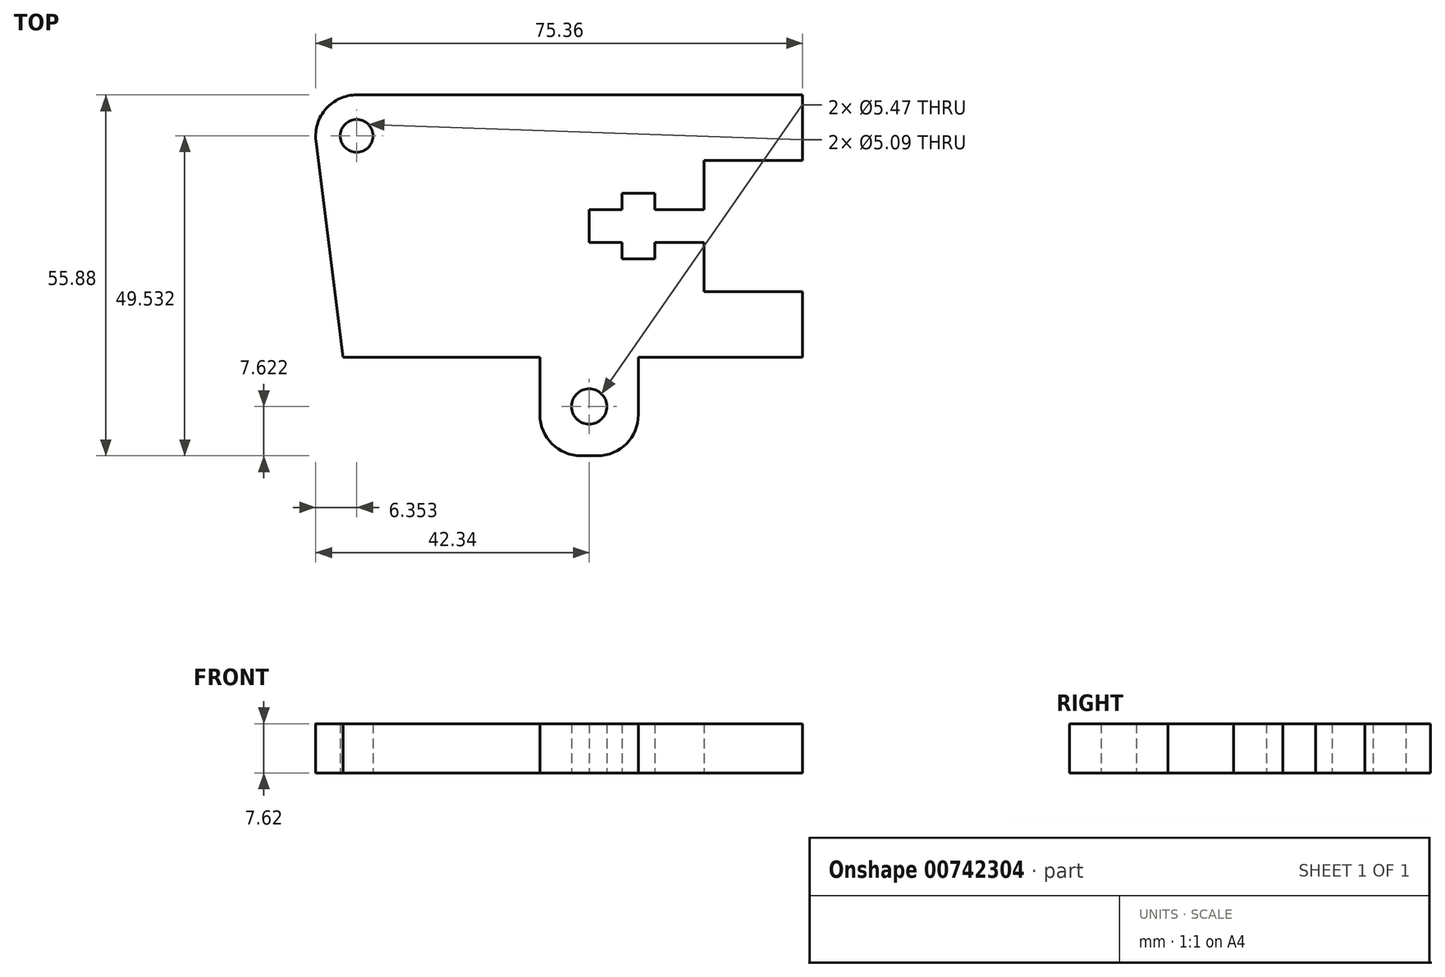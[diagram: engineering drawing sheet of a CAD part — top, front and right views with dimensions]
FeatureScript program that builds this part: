
annotation { "Feature Type Name" : "Feature", "Feature Type Description" : "" }
export const myFeature = defineFeature(function(context is Context, id is Id, definition is map)
    precondition{}
    {
        {
            var Q0;
            Q0=qCreatedBy(makeId("Top.planeOp"),FACE);
            var sketch = newSketch(context, id + "F0", { "sketchPlane" : qUnion([Q0])});
            skLineSegment(sketch, "E0", {"start": v(-53.77, 42.2) * mm, "end": v(15.24, 42.2) * mm});
            skLineSegment(sketch, "E1", {"start": v(15.24, 42.2) * mm, "end": v(15.24, 32.03) * mm});
            skLineSegment(sketch, "E2", {"start": v(15.24, 32.03) * mm, "end": v(0, 32.03) * mm});
            skLineSegment(sketch, "E3", {"start": v(0, 32.03) * mm, "end": v(0, 24.41) * mm});
            skLineSegment(sketch, "E4", {"start": v(0, 24.41) * mm, "end": v(-7.62, 24.41) * mm});
            skLineSegment(sketch, "E5", {"start": v(-12.7, 24.41) * mm, "end": v(-17.78, 24.41) * mm});
            skLineSegment(sketch, "E6", {"start": v(-17.78, 24.41) * mm, "end": v(-17.78, 19.33) * mm});
            skLineSegment(sketch, "E7", {"start": v(-17.78, 19.33) * mm, "end": v(-12.7, 19.33) * mm});
            skLineSegment(sketch, "E8", {"start": v(-12.7, 19.33) * mm, "end": v(-12.7, 16.8) * mm});
            skLineSegment(sketch, "E9", {"start": v(-12.7, 16.8) * mm, "end": v(-7.62, 16.8) * mm});
            skLineSegment(sketch, "E10", {"start": v(-7.62, 16.8) * mm, "end": v(-7.62, 19.33) * mm});
            skLineSegment(sketch, "E11", {"start": v(-7.62, 19.33) * mm, "end": v(0, 19.33) * mm});
            skLineSegment(sketch, "E12", {"start": v(0, 19.33) * mm, "end": v(0, 11.71) * mm});
            skLineSegment(sketch, "E13", {"start": v(0, 11.71) * mm, "end": v(15.24, 11.71) * mm});
            skLineSegment(sketch, "E14", {"start": v(15.24, 11.71) * mm, "end": v(15.24, 1.55) * mm});
            skLineSegment(sketch, "E15", {"start": v(15.24, 1.55) * mm, "end": v(-10.16, 1.55) * mm});
            skLineSegment(sketch, "E16", {"start": v(-10.16, 1.55) * mm, "end": v(-10.16, -7.34) * mm});
            skLineSegment(sketch, "E17", {"start": v(-16.51, -13.69) * mm, "end": v(-19.05, -13.69) * mm});
            skLineSegment(sketch, "E18", {"start": v(-25.4, -7.34) * mm, "end": v(-25.4, 1.55) * mm});
            skLineSegment(sketch, "E19", {"start": v(-25.4, 1.55) * mm, "end": v(-55.88, 1.55) * mm});
            skLineSegment(sketch, "E20", {"start": v(-55.88, 1.55) * mm, "end": v(-60.07, 35.05) * mm});
            skLineSegment(sketch, "E21", {"start": v(-7.62, 24.41) * mm, "end": v(-7.62, 26.95) * mm});
            skLineSegment(sketch, "E22", {"start": v(-7.62, 26.95) * mm, "end": v(-12.7, 26.95) * mm});
            skLineSegment(sketch, "E23", {"start": v(-12.7, 26.95) * mm, "end": v(-12.7, 24.41) * mm});
            skCircle(sketch, "E24", {"center": v(-17.78, -6.07) * mm, "radius": 2.73 * mm});
            skPoint(sketch, "E24.centerSnap0", {"position": v(-17.78, -13.69) * mm});
            skPoint(sketch, "E24.centerSnap1", {"position": v(-25.4, -6.07) * mm});
            skPoint(sketch, "E25.visualSharp", {"position": v(-25.4, -13.69) * mm});
            skArc(sketch, "E25.filletArc", {"start": v(-25.4, -7.34) * mm, "mid": v(-23.54, -11.83) * mm, "end": v(-19.05, -13.69) * mm});
            skPoint(sketch, "E26.visualSharp", {"position": v(-10.16, -13.69) * mm});
            skArc(sketch, "E26.filletArc", {"start": v(-16.51, -13.69) * mm, "mid": v(-12.02, -11.83) * mm, "end": v(-10.16, -7.34) * mm});
            skPoint(sketch, "E27.visualSharp", {"position": v(-60.96, 42.2) * mm});
            skArc(sketch, "E27.filletArc", {"start": v(-53.77, 42.2) * mm, "mid": v(-58.53, 40.04) * mm, "end": v(-60.07, 35.05) * mm});
            skCircle(sketch, "E28", {"center": v(-53.77, 35.84) * mm, "radius": 2.54 * mm});
            skSolve(sketch);
        }
        {
            var Q0;
            Q0 = qSketchRegion(id + "F0", true);
            extrude(context, id + "F1", {"entities" : qUnion([Q0]), "depth" : 7.62 * mm, "offsetDistance" : 25.4 * mm});
        }
    });
